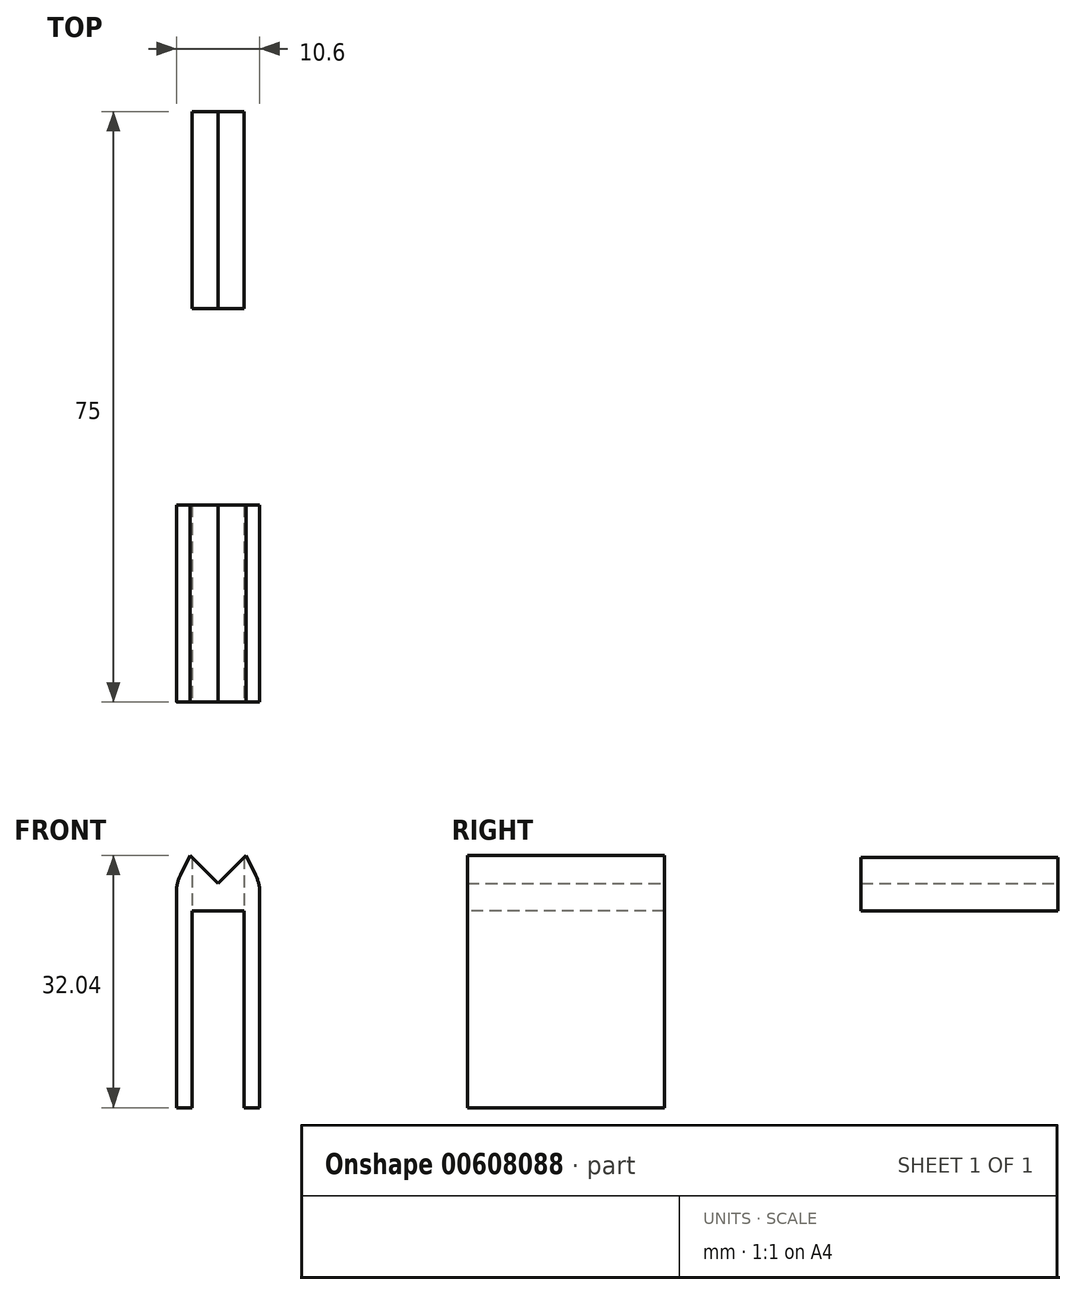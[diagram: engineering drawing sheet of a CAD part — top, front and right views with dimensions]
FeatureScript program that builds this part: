
annotation { "Feature Type Name" : "Feature", "Feature Type Description" : "" }
export const myFeature = defineFeature(function(context is Context, id is Id, definition is map)
    precondition{}
    {
        {
            var Q0;
            Q0=qCreatedBy(makeId("Top.planeOp"),FACE);
            var sketch = newSketch(context, id + "F0", { "sketchPlane" : qUnion([Q0])});
            skLineSegment(sketch, "E0.bottom", {"start": v(-3.3, 12.5) * mm, "end": v(3.3, 12.5) * mm});
            skLineSegment(sketch, "E0.top", {"start": v(-3.3, -12.5) * mm, "end": v(3.3, -12.5) * mm});
            skLineSegment(sketch, "E0.left", {"start": v(-3.3, 12.5) * mm, "end": v(-3.3, -12.5) * mm});
            skLineSegment(sketch, "E0.right", {"start": v(3.3, 12.5) * mm, "end": v(3.3, -12.5) * mm});
            skPoint(sketch, "E0.middle", {"position": v(0, 0) * mm});
            skLineSegment(sketch, "E1.bottom", {"start": v(-3.3, 12.5) * mm, "end": v(-5.3, 12.5) * mm});
            skLineSegment(sketch, "E1.top", {"start": v(-3.3, -12.5) * mm, "end": v(-5.3, -12.5) * mm});
            skLineSegment(sketch, "E1.right", {"start": v(-5.3, 12.5) * mm, "end": v(-5.3, -12.5) * mm});
            skLineSegment(sketch, "E2.bottom", {"start": v(3.3, 12.5) * mm, "end": v(5.3, 12.5) * mm});
            skLineSegment(sketch, "E2.top", {"start": v(3.3, -12.5) * mm, "end": v(5.3, -12.5) * mm});
            skLineSegment(sketch, "E2.right", {"start": v(5.3, 12.5) * mm, "end": v(5.3, -12.5) * mm});
            skSolve(sketch);
        }
        {
            var Q0;
            Q0=makeQuery(id+"F0.imprint","IMPRINT",FACE,{"disambiguationData":[TD([[makeQuery(id+"F0.imprint","IMPRINT",EDGE,{"derivedFrom":sQuery(id+"F0.wireOp",EDGE,"E1.bottom")}),1.0]])]});
            var Q1;
            Q1=makeQuery(id+"F0.imprint","IMPRINT",FACE,{"disambiguationData":[TD([[makeQuery(id+"F0.imprint","IMPRINT",EDGE,{"derivedFrom":sQuery(id+"F0.wireOp",EDGE,"E0.bottom")}),-1.0]])]});
            var Q2;
            Q2=makeQuery(id+"F0.imprint","IMPRINT",FACE,{"disambiguationData":[TD([[makeQuery(id+"F0.imprint","IMPRINT",EDGE,{"derivedFrom":sQuery(id+"F0.wireOp",EDGE,"E2.bottom")}),-1.0]])]});
            extrude(context, id + "F1", {"entities" : qUnion([Q0, Q1, Q2]), "depth" : 3.5 * mm, "offsetDistance" : 25 * mm});
        }
        {
            var Q0;
            Q0=makeQuery(id+"F0.imprint","IMPRINT",FACE,{"disambiguationData":[TD([[makeQuery(id+"F0.imprint","IMPRINT",EDGE,{"derivedFrom":sQuery(id+"F0.wireOp",EDGE,"E1.bottom")}),1.0]])]});
            var Q1;
            Q1=makeQuery(id+"F0.imprint","IMPRINT",FACE,{"disambiguationData":[TD([[makeQuery(id+"F0.imprint","IMPRINT",EDGE,{"derivedFrom":sQuery(id+"F0.wireOp",EDGE,"E2.bottom")}),-1.0]])]});
            extrude(context, id + "F2", {"entities" : qUnion([Q0, Q1]), "operationType" : NewBodyOperationType.ADD, "oppositeDirection" : true, "depth" : 25 * mm, "offsetDistance" : 25 * mm});
        }
        {
            var Q0;
            Q0=qCreatedBy(makeId("Front.planeOp"),FACE);
            var sketch = newSketch(context, id + "F3", { "sketchPlane" : qUnion([Q0])});
            skLineSegment(sketch, "E3.0", {"start": v(5.3, 3.5) * mm, "end": v(-5.3, 3.5) * mm});
            skLineSegment(sketch, "E4", {"start": v(0, 3.5) * mm, "end": v(-3.54, 7.04) * mm});
            skLineSegment(sketch, "E5", {"start": v(0, 3.5) * mm, "end": v(3.54, 7.04) * mm});
            skLineSegment(sketch, "E6", {"start": v(3.54, 7.04) * mm, "end": v(5.3, 3.5) * mm});
            skLineSegment(sketch, "E7", {"start": v(-3.54, 7.04) * mm, "end": v(-5.3, 3.5) * mm});
            skSolve(sketch);
        }
        {
            var Q0;
            {var subQ2=sQuery(id+"F3.wireOp",EDGE,"E5");Q0=makeQuery(id+"F3.imprint","IMPRINT",FACE,{"disambiguationData":[TD([[makeQuery(id+"F3.imprint","IMPRINT",EDGE,{"derivedFrom":subQ2}),-1.0]])]});}
            var Q1;
            {var subQ2=sQuery(id+"F3.wireOp",EDGE,"E4");Q1=makeQuery(id+"F3.imprint","IMPRINT",FACE,{"disambiguationData":[TD([[makeQuery(id+"F3.imprint","IMPRINT",EDGE,{"derivedFrom":subQ2}),1.0]])]});}
            var Q2;
            {var subQ0=sQuery(id+"F0.wireOp",EDGE,"E2.top");var subQ1=sQuery(id+"F0.wireOp",EDGE,"E1.top");Q2=makeQuery(id+"F2.boolean.opBoolean","MERGE",FACE,{"derivedFrom":[makeQuery(id+"F1.opExtrude","SWEPT_FACE",FACE,{"disambiguationData":[OSD([sQuery(id+"F0.wireOp",EDGE,"E0.top"),subQ1,subQ0])]}),makeQuery(id+"F2.opExtrude","SWEPT_FACE",FACE,{"disambiguationData":[OSD([subQ1])]}),makeQuery(id+"F2.opExtrude","SWEPT_FACE",FACE,{"disambiguationData":[OSD([subQ0])]})]});}
            var Q3;
            {var subQ0=sQuery(id+"F0.wireOp",EDGE,"E2.bottom");var subQ1=sQuery(id+"F0.wireOp",EDGE,"E1.bottom");Q3=makeQuery(id+"F2.boolean.opBoolean","MERGE",FACE,{"derivedFrom":[makeQuery(id+"F1.opExtrude","SWEPT_FACE",FACE,{"disambiguationData":[OSD([sQuery(id+"F0.wireOp",EDGE,"E0.bottom"),subQ1,subQ0])]}),makeQuery(id+"F2.opExtrude","SWEPT_FACE",FACE,{"disambiguationData":[OSD([subQ1])]}),makeQuery(id+"F2.opExtrude","SWEPT_FACE",FACE,{"disambiguationData":[OSD([subQ0])]})]});}
            extrude(context, id + "F4", {"entities" : qUnion([Q0, Q1]), "operationType" : NewBodyOperationType.ADD, "endBound" : BoundingType.UP_TO_SURFACE, "depth" : 11 * mm, "endBoundEntityFace" : qUnion([Q2]), "offsetDistance" : 25 * mm, "hasSecondDirection" : true, "secondDirectionBound" : SecondDirectionBoundingType.UP_TO_SURFACE, "secondDirectionOppositeDirection" : true, "secondDirectionDepth" : 25 * mm, "secondDirectionBoundEntityFace" : qUnion([Q3])});
        }
        {
            var Q0;
            {var subQ0=sQuery(id+"F3.wireOp",EDGE,"E7");var subQ1=sQuery(id+"F3.wireOp",EDGE,"E3.0");Q0=makeQuery(id+"F4.boolean.opBoolean","MERGE",EDGE,{"derivedFrom":[makeQuery(id+"F1.opExtrude","CAP_EDGE",EDGE,{"disambiguationData":[OSD([sQuery(id+"F0.wireOp",EDGE,"E1.right")])],"isStart":false}),makeQuery(id+"F4.opExtrude","TWEAK_EDGE",EDGE,{"derivedFrom":[makeQuery(id+"F3.imprint","IMPRINT",EDGE,{"disambiguationData":[TD([[makeQuery(id+"F3.imprint","INTERSECT",VERTEX,{"derivedFrom":[subQ1,subQ0]}),1.0]])],"derivedFrom":subQ1}),makeQuery(id+"F3.imprint","IMPRINT",EDGE,{"derivedFrom":subQ0})]})]});}
            var Q1;
            {var subQ0=sQuery(id+"F3.wireOp",EDGE,"E6");var subQ1=sQuery(id+"F3.wireOp",EDGE,"E3.0");Q1=makeQuery(id+"F4.boolean.opBoolean","MERGE",EDGE,{"derivedFrom":[makeQuery(id+"F1.opExtrude","CAP_EDGE",EDGE,{"disambiguationData":[OSD([sQuery(id+"F0.wireOp",EDGE,"E2.right")])],"isStart":false}),makeQuery(id+"F4.opExtrude","TWEAK_EDGE",EDGE,{"derivedFrom":[makeQuery(id+"F3.imprint","IMPRINT",EDGE,{"disambiguationData":[TD([[makeQuery(id+"F3.imprint","INTERSECT",VERTEX,{"derivedFrom":[subQ1,subQ0]}),-1.0]])],"derivedFrom":subQ1}),makeQuery(id+"F3.imprint","IMPRINT",EDGE,{"derivedFrom":subQ0})]})]});}
            fillet(context, id + "F5", {"entities" : qUnion([Q0, Q1]), "radius" : 5 * mm, "tangentPropagation" : true, "allowEdgeOverflow" : false});
        }
        {
            var Q0;
            Q0=makeQuery(id+"F1.opExtrude","SWEPT_BODY",BODY,{"disambiguationData":[OSD([sQuery(id+"F0.wireOp",EDGE,"E0.bottom"),sQuery(id+"F0.wireOp",EDGE,"E0.top"),sQuery(id+"F0.wireOp",EDGE,"E1.bottom"),sQuery(id+"F0.wireOp",EDGE,"E1.top"),sQuery(id+"F0.wireOp",EDGE,"E1.right"),sQuery(id+"F0.wireOp",EDGE,"E2.bottom"),sQuery(id+"F0.wireOp",EDGE,"E2.top"),sQuery(id+"F0.wireOp",EDGE,"E2.right")])]});
            transform(context, id + "F6", {"entities" : qUnion([Q0]), "transformType" : TransformType.TRANSLATION_3D, "dx" : 0 * mm, "dy" : 50 * mm, "dz" : 0 * mm, "makeCopy" : true});
        }
        {
            var Q0;
            {var subQ0=sQuery(id+"F0.wireOp",EDGE,"E2.right");Q0=makeQuery(id+"F6.opPattern","COPY",FACE,{"derivedFrom":makeQuery(id+"F2.boolean.opBoolean","MERGE",FACE,{"derivedFrom":[makeQuery(id+"F1.opExtrude","SWEPT_FACE",FACE,{"disambiguationData":[OSD([subQ0])]}),makeQuery(id+"F2.opExtrude","SWEPT_FACE",FACE,{"disambiguationData":[OSD([subQ0])]})]}),"instanceName":"1"});}
            var sketch = newSketch(context, id + "F7", { "sketchPlane" : qUnion([Q0])});
            skLineSegment(sketch, "E8.bottom", {"start": v(37.5, -25) * mm, "end": v(62.5, -25) * mm});
            skLineSegment(sketch, "E8.top", {"start": v(37.5, -5) * mm, "end": v(62.5, -5) * mm});
            skLineSegment(sketch, "E8.left", {"start": v(37.5, -25) * mm, "end": v(37.5, -5) * mm});
            skLineSegment(sketch, "E8.right", {"start": v(62.5, -25) * mm, "end": v(62.5, -5) * mm});
            skSolve(sketch);
        }
        {
            var Q0;
            Q0=makeQuery(id+"F7.imprint","IMPRINT",FACE,{"disambiguationData":[TD([[makeQuery(id+"F7.imprint","IMPRINT",EDGE,{"derivedFrom":sQuery(id+"F7.wireOp",EDGE,"E8.bottom")}),-1.0]])]});
            extrude(context, id + "F8", {"entities" : qUnion([Q0]), "operationType" : NewBodyOperationType.REMOVE, "oppositeDirection" : true, "depth" : 25 * mm, "offsetDistance" : 25 * mm});
        }
        {
            var Q0;
            {var subQ0=sQuery(id+"F0.wireOp",EDGE,"E2.bottom");var subQ1=sQuery(id+"F0.wireOp",EDGE,"E1.bottom");var subQ2=sQuery(id+"F0.wireOp",EDGE,"E0.bottom");Q0=makeQuery(id+"F6.opPattern","COPY",FACE,{"derivedFrom":makeQuery(id+"F4.boolean.opBoolean","MERGE",FACE,{"derivedFrom":[makeQuery(id+"F2.boolean.opBoolean","MERGE",FACE,{"derivedFrom":[makeQuery(id+"F1.opExtrude","SWEPT_FACE",FACE,{"disambiguationData":[OSD([subQ2,subQ1,subQ0])]}),makeQuery(id+"F2.opExtrude","SWEPT_FACE",FACE,{"disambiguationData":[OSD([subQ1])]}),makeQuery(id+"F2.opExtrude","SWEPT_FACE",FACE,{"disambiguationData":[OSD([subQ0])]})]}),makeQuery(id+"F4.opExtrude","CAP_FACE",FACE,{"disambiguationData":[OSD([subQ2,subQ1,subQ0]),OD(0.0)],"isStart":true}),makeQuery(id+"F4.opExtrude","CAP_FACE",FACE,{"disambiguationData":[OSD([subQ2,subQ1,subQ0]),OD(1.0)],"isStart":true})]}),"instanceName":"1"});}
            var sketch = newSketch(context, id + "F9", { "sketchPlane" : qUnion([Q0])});
            skPoint(sketch, "E9.oppositeSnap0", {"position": v(-3.3, -2.5) * mm});
            skLineSegment(sketch, "E9.bottom", {"start": v(-5.3, -5) * mm, "end": v(-3.3, -5) * mm});
            skLineSegment(sketch, "E9.top", {"start": v(-5.3, 9.05) * mm, "end": v(-3.3, 9.05) * mm});
            skLineSegment(sketch, "E9.left", {"start": v(-5.3, -5) * mm, "end": v(-5.3, 9.05) * mm});
            skLineSegment(sketch, "E9.right", {"start": v(-3.3, -5) * mm, "end": v(-3.3, 9.05) * mm});
            skPoint(sketch, "E10.oppositeSnap0", {"position": v(5.3, -1.34) * mm});
            skLineSegment(sketch, "E10.bottom", {"start": v(3.3, -5) * mm, "end": v(5.3, -5) * mm});
            skLineSegment(sketch, "E10.top", {"start": v(3.3, 8.04) * mm, "end": v(5.3, 8.04) * mm});
            skLineSegment(sketch, "E10.left", {"start": v(3.3, -5) * mm, "end": v(3.3, 8.04) * mm});
            skLineSegment(sketch, "E10.right", {"start": v(5.3, -5) * mm, "end": v(5.3, 8.04) * mm});
            skSolve(sketch);
        }
        {
            var Q0;
            {var subQ5=sQuery(id+"F9.wireOp",EDGE,"E9.bottom");Q0=makeQuery(id+"F9.imprint","IMPRINT",FACE,{"disambiguationData":[TD([[makeQuery(id+"F9.imprint","IMPRINT",EDGE,{"derivedFrom":subQ5}),-1.0]])]});}
            var Q1;
            {var subQ10=sQuery(id+"F9.wireOp",EDGE,"E10.bottom");Q1=makeQuery(id+"F9.imprint","IMPRINT",FACE,{"disambiguationData":[TD([[makeQuery(id+"F9.imprint","IMPRINT",EDGE,{"derivedFrom":subQ10}),-1.0]])]});}
            extrude(context, id + "F10", {"entities" : qUnion([Q0, Q1]), "operationType" : NewBodyOperationType.REMOVE, "oppositeDirection" : true, "depth" : 27.2 * mm, "offsetDistance" : 25 * mm});
        }
    });
